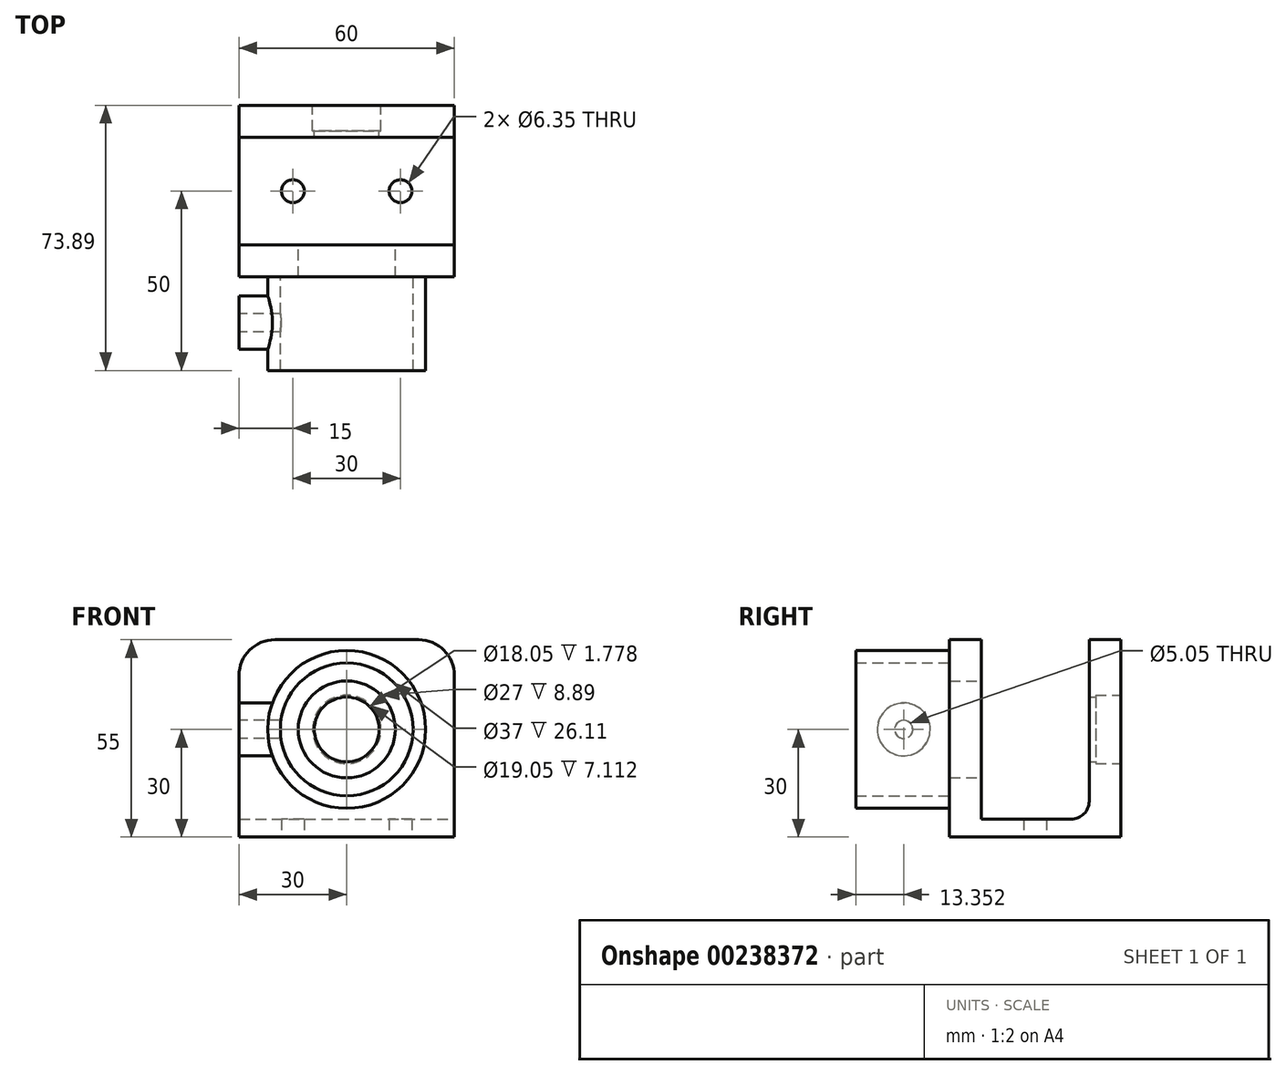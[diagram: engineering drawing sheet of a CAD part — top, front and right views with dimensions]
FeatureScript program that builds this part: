
annotation { "Feature Type Name" : "Feature", "Feature Type Description" : "" }
export const myFeature = defineFeature(function(context is Context, id is Id, definition is map)
    precondition{}
    {
        {
            var Q0;
            Q0=qCreatedBy(makeId("Front.planeOp"),FACE);
            var sketch = newSketch(context, id + "F0", { "sketchPlane" : qUnion([Q0])});
            skCircle(sketch, "E0", {"center": v(0, 0) * mm, "radius": 18.5 * mm});
            skCircle(sketch, "E1", {"center": v(0, 0) * mm, "radius": 13.5 * mm});
            skLineSegment(sketch, "E2.right", {"start": v(30, 25) * mm, "end": v(30, -25) * mm});
            skLineSegment(sketch, "E3", {"start": v(30, 25) * mm, "end": v(-30, 25) * mm});
            skLineSegment(sketch, "E4", {"start": v(-30, 25) * mm, "end": v(-30, -25) * mm});
            skLineSegment(sketch, "E5", {"start": v(-30, -25) * mm, "end": v(30, -25) * mm});
            skLineSegment(sketch, "E6", {"start": v(30, -25) * mm, "end": v(30, -30) * mm});
            skLineSegment(sketch, "E7", {"start": v(-30, -25) * mm, "end": v(-30, -30) * mm});
            skLineSegment(sketch, "E8", {"start": v(-30, -30) * mm, "end": v(30, -30) * mm});
            skCircle(sketch, "E9", {"center": v(0, 0) * mm, "radius": 22 * mm});
            skSolve(sketch);
        }
        {
            var Q0;
            Q0=makeQuery(id+"F0.imprint","IMPRINT",FACE,{"disambiguationData":[TD([[makeQuery(id+"F0.imprint","IMPRINT",EDGE,{"derivedFrom":sQuery(id+"F0.wireOp",EDGE,"E5")}),-1.0]])]});
            var Q1;
            Q1=makeQuery(id+"F0.imprint","IMPRINT",FACE,{"disambiguationData":[TD([[makeQuery(id+"F0.imprint","IMPRINT",EDGE,{"derivedFrom":sQuery(id+"F0.wireOp",EDGE,"E2.right")}),-1.0]])]});
            var Q2;
            Q2=makeQuery(id+"F0.imprint","IMPRINT",FACE,{"disambiguationData":[TD([[makeQuery(id+"F0.imprint","IMPRINT",EDGE,{"derivedFrom":sQuery(id+"F0.wireOp",EDGE,"E0")}),1.0]])]});
            var Q3;
            Q3=makeQuery(id+"F0.imprint","IMPRINT",FACE,{"disambiguationData":[TD([[makeQuery(id+"F0.imprint","IMPRINT",EDGE,{"derivedFrom":sQuery(id+"F0.wireOp",EDGE,"E0")}),-1.0]])]});
            extrude(context, id + "F1", {"entities" : qUnion([Q0, Q1, Q2, Q3]), "depth" : 8.9 * mm});
        }
        {
            var Q0;
            Q0=makeQuery(id+"F0.imprint","IMPRINT",FACE,{"disambiguationData":[TD([[makeQuery(id+"F0.imprint","IMPRINT",EDGE,{"derivedFrom":sQuery(id+"F0.wireOp",EDGE,"E0")}),-1.0]])]});
            extrude(context, id + "F2", {"entities" : qUnion([Q0]), "operationType" : NewBodyOperationType.ADD, "depth" : 35 * mm});
        }
        {
            var Q0;
            Q0=makeQuery(id+"F1.opExtrude","SWEPT_FACE",FACE,{"disambiguationData":[OSD([sQuery(id+"F0.wireOp",EDGE,"E2.right"),sQuery(id+"F0.wireOp",EDGE,"E6")])]});
            var sketch = newSketch(context, id + "F3", { "sketchPlane" : qUnion([Q0])});
            skLineSegment(sketch, "E10", {"start": v(0, -30) * mm, "end": v(30, -30) * mm});
            skLineSegment(sketch, "E11", {"start": v(30, -30) * mm, "end": v(30, -25) * mm});
            skLineSegment(sketch, "E12", {"start": v(30, -25) * mm, "end": v(0, -25) * mm});
            skLineSegment(sketch, "E13", {"start": v(0, -25) * mm, "end": v(0, -30) * mm});
            skLineSegment(sketch, "E14.bottom", {"start": v(30, -30) * mm, "end": v(38.9, -30) * mm});
            skLineSegment(sketch, "E14.top", {"start": v(30, 25) * mm, "end": v(38.89, 25) * mm});
            skLineSegment(sketch, "E14.left", {"start": v(30, -30) * mm, "end": v(30, 25) * mm});
            skLineSegment(sketch, "E14.right", {"start": v(38.9, -30) * mm, "end": v(38.89, 25) * mm});
            skSolve(sketch);
        }
        {
            var Q0;
            {var subQ3=sQuery(id+"F3.wireOp",EDGE,"E14.bottom");Q0=makeQuery(id+"F3.imprint","IMPRINT",FACE,{"disambiguationData":[TD([[makeQuery(id+"F3.imprint","IMPRINT",EDGE,{"derivedFrom":subQ3}),1.0]])]});}
            var Q1;
            {var subQ0=sQuery(id+"F3.wireOp",EDGE,"E10");Q1=makeQuery(id+"F3.imprint","IMPRINT",FACE,{"disambiguationData":[TD([[makeQuery(id+"F3.imprint","IMPRINT",EDGE,{"derivedFrom":subQ0}),1.0]])]});}
            extrude(context, id + "F4", {"entities" : qUnion([Q0, Q1]), "operationType" : NewBodyOperationType.ADD, "oppositeDirection" : true, "depth" : 60 * mm});
        }
        {
            var Q0;
            Q0=makeQuery(id+"F4.opExtrude","SWEPT_EDGE",EDGE,{"disambiguationData":[OSD([sQuery(id+"F3.wireOp",EDGE,"E12"),sQuery(id+"F3.wireOp",EDGE,"E14.left")])]});
            var Q1;
            Q1=makeQuery(id+"F4.opExtrude","SWEPT_EDGE",EDGE,{"disambiguationData":[OSD([sQuery(id+"F0.wireOp",EDGE,"E2.right"),sQuery(id+"F0.wireOp",EDGE,"E6"),sQuery(id+"F3.wireOp",EDGE,"E12"),sQuery(id+"F3.wireOp",EDGE,"E13")])]});
            fillet(context, id + "F5", {"entities" : qUnion([Q0, Q1]), "radius" : 5 * mm, "tangentPropagation" : true, "allowEdgeOverflow" : false});
        }
        {
            var Q0;
            Q0=makeQuery(id+"F4.opExtrude","SWEPT_FACE",FACE,{"disambiguationData":[OSD([sQuery(id+"F3.wireOp",EDGE,"E14.right")])]});
            var sketch = newSketch(context, id + "F6", { "sketchPlane" : qUnion([Q0])});
            skCircle(sketch, "E15", {"center": v(0, 0) * mm, "radius": 9.03 * mm});
            skCircle(sketch, "E16", {"center": v(0, 0) * mm, "radius": 9.53 * mm});
            skSolve(sketch);
        }
        {
            var Q0;
            Q0=makeQuery(id+"F6.imprint","IMPRINT",FACE,{"disambiguationData":[TD([[makeQuery(id+"F6.imprint","IMPRINT",EDGE,{"derivedFrom":sQuery(id+"F6.wireOp",EDGE,"E15")}),1.0]])]});
            extrude(context, id + "F7", {"entities" : qUnion([Q0]), "operationType" : NewBodyOperationType.REMOVE, "oppositeDirection" : true, "depth" : 7.11 * mm});
        }
        {
            var Q0;
            Q0=makeQuery(id+"F6.imprint","IMPRINT",FACE,{"disambiguationData":[TD([[makeQuery(id+"F6.imprint","IMPRINT",EDGE,{"derivedFrom":sQuery(id+"F6.wireOp",EDGE,"E15")}),1.0]])]});
            extrude(context, id + "F8", {"entities" : qUnion([Q0]), "operationType" : NewBodyOperationType.REMOVE, "oppositeDirection" : true, "depth" : 25 * mm});
        }
        {
            var Q0;
            Q0=makeQuery(id+"F6.imprint","IMPRINT",FACE,{"disambiguationData":[TD([[makeQuery(id+"F6.imprint","IMPRINT",EDGE,{"derivedFrom":sQuery(id+"F6.wireOp",EDGE,"E15")}),-1.0]])]});
            var Q1;
            Q1=sQuery(id+"F6.wireOp",EDGE,"E16");
            extrude(context, id + "F9", {"entities" : qUnion([Q0]), "operationType" : NewBodyOperationType.REMOVE, "surfaceEntities" : qUnion([Q1]), "oppositeDirection" : true, "depth" : 7.11 * mm});
        }
        {
            var Q0;
            Q0=makeQuery(id+"F1.opExtrude","SWEPT_EDGE",EDGE,{"disambiguationData":[OSD([sQuery(id+"F0.wireOp",EDGE,"E2.right"),sQuery(id+"F0.wireOp",EDGE,"E3")])]});
            var Q1;
            Q1=makeQuery(id+"F4.opExtrude","CAP_EDGE",EDGE,{"disambiguationData":[OSD([sQuery(id+"F3.wireOp",EDGE,"E14.top")])],"isStart":true});
            var Q2;
            Q2=makeQuery(id+"F1.opExtrude","SWEPT_EDGE",EDGE,{"disambiguationData":[OSD([sQuery(id+"F0.wireOp",EDGE,"E3"),sQuery(id+"F0.wireOp",EDGE,"E4")])]});
            var Q3;
            Q3=makeQuery(id+"F4.opExtrude","CAP_EDGE",EDGE,{"disambiguationData":[OSD([sQuery(id+"F3.wireOp",EDGE,"E14.top")])],"isStart":false});
            fillet(context, id + "F10", {"entities" : qUnion([Q0, Q1, Q2, Q3]), "radius" : 10 * mm, "tangentPropagation" : true, "allowEdgeOverflow" : false});
        }
        {
            var Q0;
            Q0=qCreatedBy(makeId("Right.planeOp"),FACE);
            var sketch = newSketch(context, id + "F11", { "sketchPlane" : qUnion([Q0])});
            skLineSegment(sketch, "E17.0", {"start": v(-35, -22) * mm, "end": v(-35, 22) * mm});
            skLineSegment(sketch, "E18.0", {"start": v(-8.9, 15) * mm, "end": v(-8.9, -30) * mm});
            skLineSegment(sketch, "E19", {"start": v(-8.9, -22.35) * mm, "end": v(-35, -22) * mm});
            skLineSegment(sketch, "E20", {"start": v(-21.95, -22.17) * mm, "end": v(-21.35, 22) * mm});
            skCircle(sketch, "E21", {"center": v(-21.65, 0) * mm, "radius": 7.39 * mm});
            skSolve(sketch);
        }
        {
            var Q0;
            {var subQ0=sQuery(id+"F11.wireOp",EDGE,"E21");var subQ1=sQuery(id+"F11.wireOp",EDGE,"E20");var subQ2=makeQuery(id+"F11.imprint","INTERSECT",VERTEX,{"disambiguationData":[OD(0.0)],"derivedFrom":[subQ1,subQ0]});Q0=makeQuery(id+"F11.imprint","IMPRINT",FACE,{"disambiguationData":[TD([[makeQuery(id+"F11.imprint","IMPRINT",EDGE,{"disambiguationData":[TD([[subQ2,-1.0]])],"derivedFrom":subQ1}),1.0]])]});}
            var Q1;
            {var subQ0=sQuery(id+"F11.wireOp",EDGE,"E21");var subQ1=sQuery(id+"F11.wireOp",EDGE,"E20");var subQ2=makeQuery(id+"F11.imprint","INTERSECT",VERTEX,{"disambiguationData":[OD(0.0)],"derivedFrom":[subQ1,subQ0]});Q1=makeQuery(id+"F11.imprint","IMPRINT",FACE,{"disambiguationData":[TD([[makeQuery(id+"F11.imprint","IMPRINT",EDGE,{"disambiguationData":[TD([[subQ2,-1.0]])],"derivedFrom":subQ1}),-1.0]])]});}
            extrude(context, id + "F12", {"entities" : qUnion([Q0, Q1]), "operationType" : NewBodyOperationType.ADD, "oppositeDirection" : true, "depth" : 30 * mm});
        }
        {
            var Q0;
            Q0=makeQuery(id+"F2.opExtrude","CAP_FACE",FACE,{"disambiguationData":[OSD([sQuery(id+"F0.wireOp",EDGE,"E0"),sQuery(id+"F0.wireOp",EDGE,"E9")])],"isStart":false});
            var sketch = newSketch(context, id + "F13", { "sketchPlane" : qUnion([Q0])});
            skCircle(sketch, "E22.0", {"center": v(0, 0) * mm, "radius": 18.5 * mm});
            skSolve(sketch);
        }
        {
            var Q0;
            Q0=makeQuery(id+"F13.imprint","IMPRINT",FACE,{"disambiguationData":[TD([[makeQuery(id+"F13.imprint","IMPRINT",EDGE,{"derivedFrom":sQuery(id+"F13.wireOp",EDGE,"E22.0")}),1.0]])]});
            extrude(context, id + "F14", {"entities" : qUnion([Q0]), "operationType" : NewBodyOperationType.REMOVE, "oppositeDirection" : true, "depth" : 22 * mm});
        }
        {
            var Q0;
            Q0=makeQuery(id+"F12.opExtrude","CAP_FACE",FACE,{"disambiguationData":[OSD([sQuery(id+"F11.wireOp",EDGE,"E21")])],"isStart":false});
            var sketch = newSketch(context, id + "F15", { "sketchPlane" : qUnion([Q0])});
            skCircle(sketch, "E23", {"center": v(21.65, 0) * mm, "radius": 2.53 * mm});
            skSolve(sketch);
        }
        {
            var Q0;
            Q0=makeQuery(id+"F15.imprint","IMPRINT",FACE,{"disambiguationData":[TD([[makeQuery(id+"F15.imprint","IMPRINT",EDGE,{"derivedFrom":sQuery(id+"F15.wireOp",EDGE,"E23")}),1.0]])]});
            var Q1;
            Q1=sQuery(id+"F15.wireOp",EDGE,"E23");
            extrude(context, id + "F16", {"entities" : qUnion([Q0]), "operationType" : NewBodyOperationType.REMOVE, "surfaceEntities" : qUnion([Q1]), "oppositeDirection" : true, "depth" : 13 * mm});
        }
        {
            var Q0;
            Q0=makeQuery(id+"F4.boolean.opBoolean","MERGE",FACE,{"derivedFrom":[makeQuery(id+"F1.opExtrude","SWEPT_FACE",FACE,{"disambiguationData":[OSD([sQuery(id+"F0.wireOp",EDGE,"E8")])]}),makeQuery(id+"F4.opExtrude","SWEPT_FACE",FACE,{"disambiguationData":[OSD([sQuery(id+"F3.wireOp",EDGE,"E10"),sQuery(id+"F3.wireOp",EDGE,"E14.bottom")])]})]});
            var sketch = newSketch(context, id + "F17", { "sketchPlane" : qUnion([Q0])});
            skCircle(sketch, "E24", {"center": v(-15, -15) * mm, "radius": 3.18 * mm});
            skCircle(sketch, "E25", {"center": v(15, -15) * mm, "radius": 3.17 * mm});
            skSolve(sketch);
        }
        {
            var Q0;
            Q0 = qSketchRegion(id + "F17", true);
            extrude(context, id + "F18", {"entities" : qUnion([Q0]), "operationType" : NewBodyOperationType.REMOVE, "oppositeDirection" : true, "depth" : 25 * mm});
        }
    });
